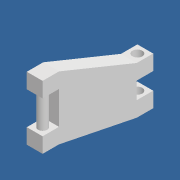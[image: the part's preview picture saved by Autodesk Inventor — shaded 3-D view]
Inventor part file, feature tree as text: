
AUTODESK INVENTOR PART (.ipt)
format: ipt  version: 2020 (Build 240168000, 168)  size: 136,192 bytes
history: native  units: mm
features: extrude x5, sketch x5
ambient origin geometry x8: Origin, YZ Plane, XZ Plane, XY Plane, X Axis, Y Axis, Z Axis, Center Point
bodies: Solid1 (feature_tree)
feature tree (10):
  extrude  "Extrusion1"  Depth=8.0mm TaperAngle=0.0deg
  extrude  "Extrusion6"  Depth=8.0mm
  extrude  "Extrusion7"  Depth=8.0mm
  extrude  "Extrusion8"  Depth=8.0mm
  extrude  "Extrusion9"  Depth=8.3mm TaperAngle=0.0deg
  sketch  "Sketch2"  dims[d4=32.0mm d7=8.0mm d8=0.0mm]
  sketch  "Sketch7"  dims[d32=24.0mm d34=8.0mm]
  sketch  "Sketch8"  dims[d35=39.4mm d36=8.0mm]
  sketch  "Sketch9"  dims[d37=7.7mm d38=8.0mm]
  sketch  "Sketch10"  dims[d39=7.7mm d40=8.3mm d41=0.0mm d42=8.0mm d43=7.7mm d44=8.0mm d45=7.7mm d46=8.3mm d47=0.0mm d48=4.6mm d49=4.0mm d50=4.0mm d51=8.3mm d52=0.0mm d53=5.0mm d54=4.0mm d55=4.0mm d56=8.3mm d57=0.0mm]
